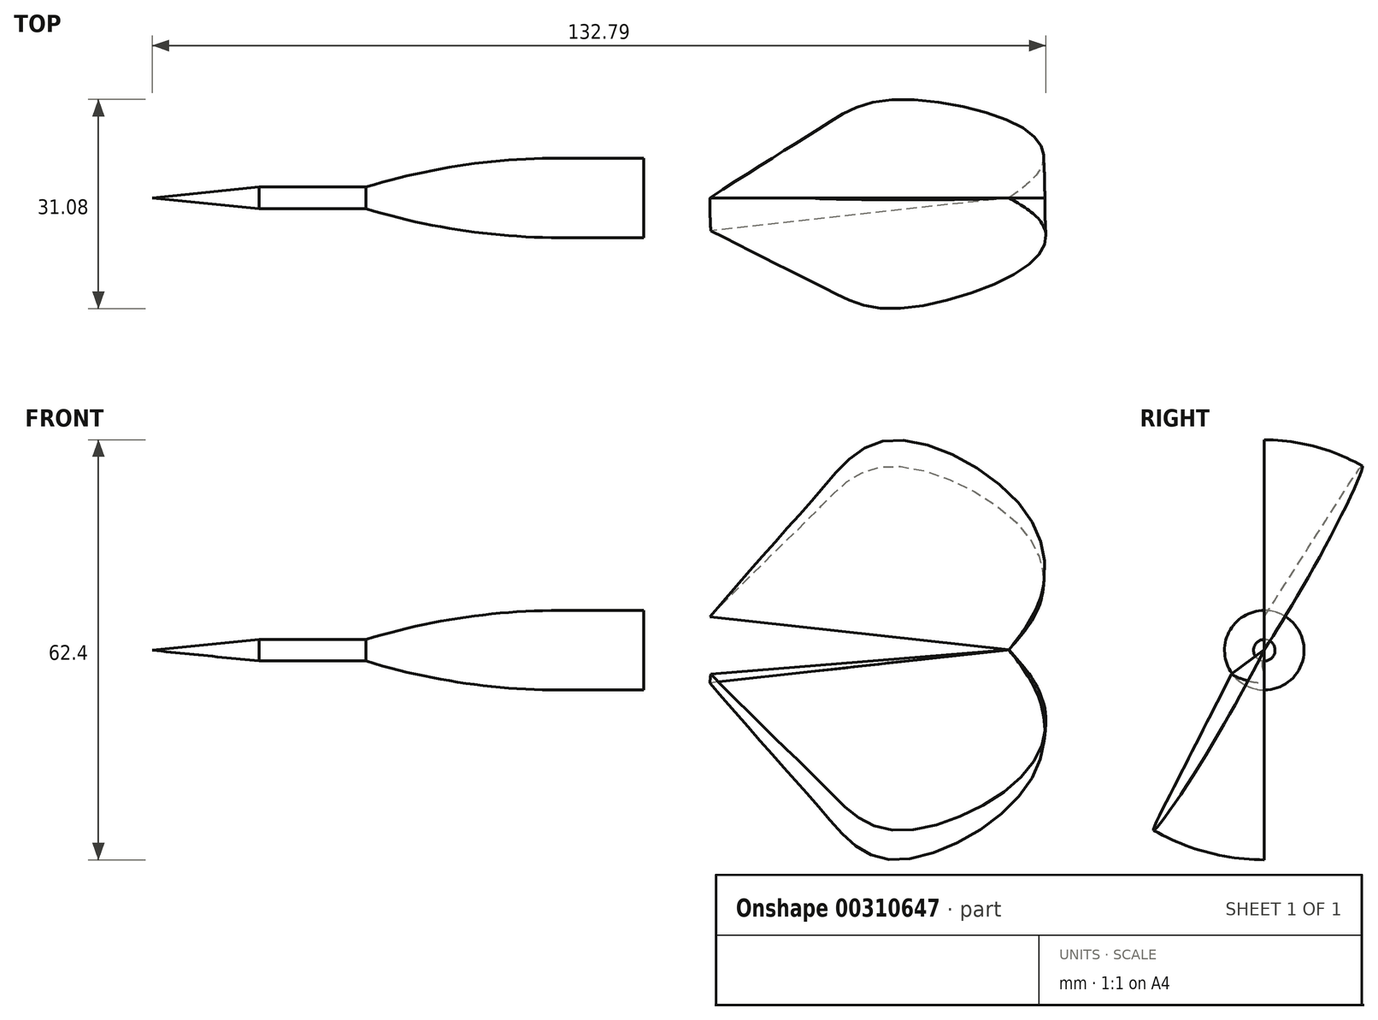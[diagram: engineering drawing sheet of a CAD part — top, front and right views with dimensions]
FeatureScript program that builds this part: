
annotation { "Feature Type Name" : "Feature", "Feature Type Description" : "" }
export const myFeature = defineFeature(function(context is Context, id is Id, definition is map)
    precondition{}
    {
        {
            var Q0;
            Q0=qCreatedBy(makeId("Front.planeOp"),FACE);
            var sketch = newSketch(context, id + "F0", { "sketchPlane" : qUnion([Q0])});
            skLineSegment(sketch, "E0", {"start": v(-101.15, -6.35) * mm, "end": v(25.85, -6.35) * mm});
            skLineSegment(sketch, "E1", {"start": v(-101.15, -6.35) * mm, "end": v(-85.28, -4.75) * mm});
            skLineSegment(sketch, "E2", {"start": v(-85.28, -4.75) * mm, "end": v(-69.4, -4.75) * mm});
            skLineSegment(sketch, "E3", {"start": v(-28.13, -0.44) * mm, "end": v(25.85, -6.35) * mm});
            skLineSegment(sketch, "E4", {"start": v(-28.13, -0.44) * mm, "end": v(-40.6, -0.44) * mm});
            skArc(sketch, "E5", {"start": v(-40.6, -0.44) * mm, "mid": v(-55.16, -1.52) * mm, "end": v(-69.4, -4.75) * mm});
            skSolve(sketch);
        }
        {
            var Q0;
            Q0=makeQuery(id+"F0.imprint","IMPRINT",FACE,{"disambiguationData":[TD([[makeQuery(id+"F0.imprint","IMPRINT",EDGE,{"derivedFrom":sQuery(id+"F0.wireOp",EDGE,"E0")}),1.0]])]});
            var Q1;
            Q1=sQuery(id+"F0.wireOp",EDGE,"E0");
            revolve(context, id + "F1", {"entities" : qUnion([Q0]), "axis" : qUnion([Q1]), "revolveType" : RevolveType.FULL});
        }
        {
            var Q0;
            Q0=qCreatedBy(makeId("Front.planeOp"),FACE);
            var sketch = newSketch(context, id + "F2", { "sketchPlane" : qUnion([Q0])});
            skLineSegment(sketch, "E6", {"start": v(26.15, -6.29) * mm, "end": v(-18.3, -1.38) * mm});
            skFitSpline(sketch, "E7", {"points": [v(-18.3, -1.38) * mm, v(-9.16, 9.12) * mm, v(-1.37, 17.93) * mm, v(8.45, 24.87) * mm, v(28.27, 14.7) * mm, v(30.97, 2) * mm, v(26.15, -6.29) * mm], "startDerivative": vector(55.2, 64) * mm, "endDerivative": vector(-41.99, -54.26) * mm});
            skFitSpline(sketch, "E8.MirrorCS", {"points": [v(-18.3, -11.2) * mm, v(-9.16, -21.7) * mm, v(-1.37, -30.5) * mm, v(8.45, -37.44) * mm, v(28.27, -27.28) * mm, v(30.97, -14.59) * mm, v(26.15, -6.29) * mm], "startDerivative": vector(55.2, -64) * mm, "endDerivative": vector(-41.99, 54.26) * mm});
            skLineSegment(sketch, "E9.MirrorCS", {"start": v(26.15, -6.29) * mm, "end": v(-18.3, -11.2) * mm});
            skLineSegment(sketch, "E10", {"start": v(26.15, -6.29) * mm, "end": v(29.8, -6.29) * mm});
            skSolve(sketch);
        }
        {
            var Q0;
            Q0=makeQuery(id+"F2.imprint","IMPRINT",FACE,{"disambiguationData":[TD([[makeQuery(id+"F2.imprint","IMPRINT",EDGE,{"derivedFrom":sQuery(id+"F2.wireOp",EDGE,"E8.MirrorCS")}),1.0]])]});
            var Q1;
            Q1=makeQuery(id+"F2.imprint","IMPRINT",FACE,{"disambiguationData":[TD([[makeQuery(id+"F2.imprint","IMPRINT",EDGE,{"derivedFrom":sQuery(id+"F2.wireOp",EDGE,"E6")}),-1.0]])]});
            var Q2;
            Q2=sQuery(id+"F2.wireOp",EDGE,"E6");
            revolve(context, id + "F3", {"operationType" : NewBodyOperationType.ADD, "entities" : qUnion([Q0, Q1]), "axis" : qUnion([Q2]), "revolveType" : RevolveType.ONE_DIRECTION, "angle" : 30 * degree});
        }
    });
